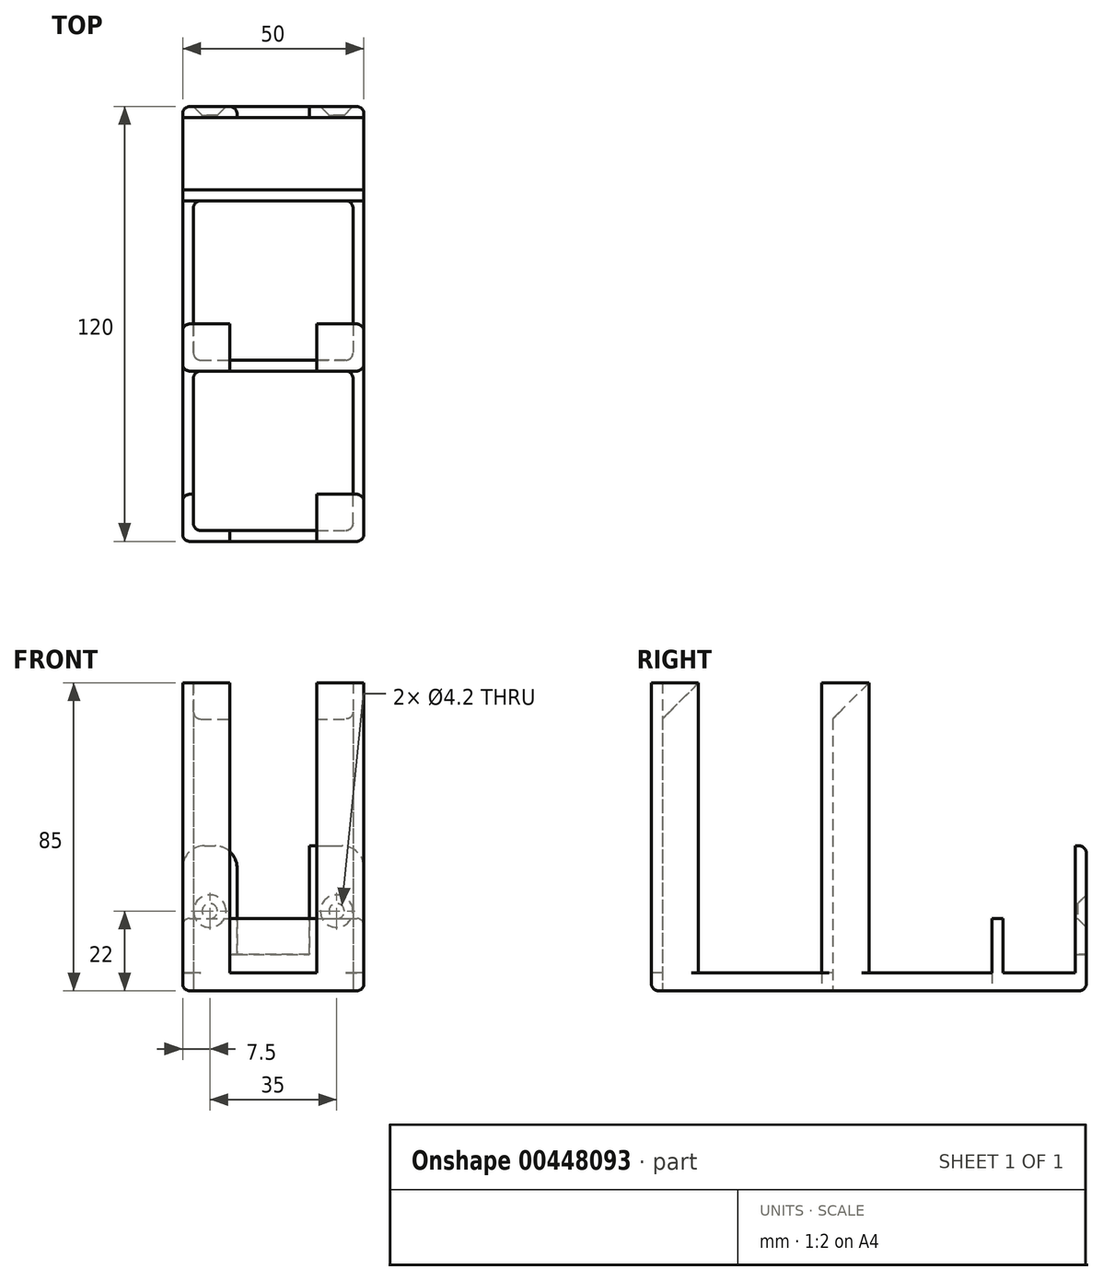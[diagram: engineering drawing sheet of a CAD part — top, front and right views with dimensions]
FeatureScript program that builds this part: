
annotation { "Feature Type Name" : "Feature", "Feature Type Description" : "" }
export const myFeature = defineFeature(function(context is Context, id is Id, definition is map)
    precondition{}
    {
        {
            var Q0;
            Q0=qCreatedBy(makeId("Top.planeOp"),FACE);
            var sketch = newSketch(context, id + "F0", { "sketchPlane" : qUnion([Q0])});
            skLineSegment(sketch, "E0.bottom", {"start": v(-22, 45.5) * mm, "end": v(22, 45.5) * mm});
            skLineSegment(sketch, "E0.top", {"start": v(-22, 1.5) * mm, "end": v(22, 1.5) * mm});
            skLineSegment(sketch, "E0.left", {"start": v(-22, 45.5) * mm, "end": v(-22, 1.5) * mm});
            skLineSegment(sketch, "E0.right", {"start": v(22, 45.5) * mm, "end": v(22, 1.5) * mm});
            skLineSegment(sketch, "E1.MirrorCS", {"start": v(-22, -1.5) * mm, "end": v(22, -1.5) * mm});
            skLineSegment(sketch, "E2.MirrorCS", {"start": v(-22, -45.5) * mm, "end": v(-22, -1.5) * mm});
            skLineSegment(sketch, "E3.MirrorCS", {"start": v(-22, -45.5) * mm, "end": v(22, -45.5) * mm});
            skLineSegment(sketch, "E4.MirrorCS", {"start": v(22, -45.5) * mm, "end": v(22, -1.5) * mm});
            skLineSegment(sketch, "E5.bottom", {"start": v(-25, 71.5) * mm, "end": v(25, 71.5) * mm});
            skLineSegment(sketch, "E5.top", {"start": v(-25, -48.5) * mm, "end": v(25, -48.5) * mm});
            skLineSegment(sketch, "E5.left", {"start": v(-25, 71.5) * mm, "end": v(-25, -48.5) * mm});
            skLineSegment(sketch, "E5.right", {"start": v(25, 71.5) * mm, "end": v(25, -48.5) * mm});
            skSolve(sketch);
        }
        {
            var Q0;
            Q0=makeQuery(id+"F0.imprint","IMPRINT",FACE,{"disambiguationData":[TD([[makeQuery(id+"F0.imprint","IMPRINT",EDGE,{"derivedFrom":sQuery(id+"F0.wireOp",EDGE,"E0.bottom")}),1.0]])]});
            extrude(context, id + "F1", {"entities" : qUnion([Q0]), "depth" : 5 * mm});
        }
        {
            var Q0;
            Q0=makeQuery(id+"F1.opExtrude","CAP_FACE",FACE,{"disambiguationData":[OSD([sQuery(id+"F0.wireOp",EDGE,"E0.bottom"),sQuery(id+"F0.wireOp",EDGE,"E0.top"),sQuery(id+"F0.wireOp",EDGE,"E0.left"),sQuery(id+"F0.wireOp",EDGE,"E0.right"),sQuery(id+"F0.wireOp",EDGE,"E1.MirrorCS"),sQuery(id+"F0.wireOp",EDGE,"E2.MirrorCS"),sQuery(id+"F0.wireOp",EDGE,"E3.MirrorCS"),sQuery(id+"F0.wireOp",EDGE,"E4.MirrorCS"),sQuery(id+"F0.wireOp",EDGE,"E5.bottom"),sQuery(id+"F0.wireOp",EDGE,"E5.top"),sQuery(id+"F0.wireOp",EDGE,"E5.left"),sQuery(id+"F0.wireOp",EDGE,"E5.right")])],"isStart":false});
            var sketch = newSketch(context, id + "F2", { "sketchPlane" : qUnion([Q0])});
            skLineSegment(sketch, "E6.bottom", {"start": v(-25, 71.5) * mm, "end": v(25, 71.5) * mm});
            skLineSegment(sketch, "E6.top", {"start": v(-25, 68.5) * mm, "end": v(25, 68.5) * mm});
            skLineSegment(sketch, "E6.left", {"start": v(-25, 71.5) * mm, "end": v(-25, 68.5) * mm});
            skLineSegment(sketch, "E6.right", {"start": v(25, 71.5) * mm, "end": v(25, 68.5) * mm});
            skLineSegment(sketch, "E7.bottom", {"start": v(-25, 48.5) * mm, "end": v(25, 48.5) * mm});
            skLineSegment(sketch, "E7.top", {"start": v(-25, 45.5) * mm, "end": v(25, 45.5) * mm});
            skLineSegment(sketch, "E7.left", {"start": v(-25, 48.5) * mm, "end": v(-25, 45.5) * mm});
            skLineSegment(sketch, "E7.right", {"start": v(25, 48.5) * mm, "end": v(25, 45.5) * mm});
            skLineSegment(sketch, "E8", {"start": v(-25, 11.5) * mm, "end": v(-22, 11.5) * mm});
            skLineSegment(sketch, "E9", {"start": v(-22, 11.5) * mm, "end": v(-22, 1.5) * mm});
            skLineSegment(sketch, "E10", {"start": v(-22, 1.5) * mm, "end": v(-12, 1.5) * mm});
            skLineSegment(sketch, "E11", {"start": v(-12, 1.5) * mm, "end": v(-12, -1.5) * mm});
            skLineSegment(sketch, "E12", {"start": v(-12, -1.5) * mm, "end": v(-25, -1.5) * mm});
            skLineSegment(sketch, "E13", {"start": v(-25, -1.5) * mm, "end": v(-25, 11.5) * mm});
            skLineSegment(sketch, "E14.MirrorCS", {"start": v(12, 1.5) * mm, "end": v(12, -1.5) * mm});
            skLineSegment(sketch, "E15.MirrorCS", {"start": v(22, 1.5) * mm, "end": v(12, 1.5) * mm});
            skLineSegment(sketch, "E16.MirrorCS", {"start": v(12, -1.5) * mm, "end": v(25, -1.5) * mm});
            skLineSegment(sketch, "E17.MirrorCS", {"start": v(25, -1.5) * mm, "end": v(25, 11.5) * mm});
            skLineSegment(sketch, "E18.MirrorCS", {"start": v(25, 11.5) * mm, "end": v(22, 11.5) * mm});
            skLineSegment(sketch, "E19.MirrorCS", {"start": v(22, 11.5) * mm, "end": v(22, 1.5) * mm});
            skLineSegment(sketch, "E20.0.1.0", {"start": v(-25, -35.5) * mm, "end": v(-22, -35.5) * mm});
            skLineSegment(sketch, "E20.0.1.1", {"start": v(-25, -48.5) * mm, "end": v(-25, -35.5) * mm});
            skLineSegment(sketch, "E20.0.1.2", {"start": v(-22, -35.5) * mm, "end": v(-22, -45.5) * mm});
            skLineSegment(sketch, "E20.0.1.3", {"start": v(-22, -45.5) * mm, "end": v(-12, -45.5) * mm});
            skLineSegment(sketch, "E20.0.1.4", {"start": v(-12, -45.5) * mm, "end": v(-12, -48.5) * mm});
            skLineSegment(sketch, "E20.0.1.5", {"start": v(-12, -48.5) * mm, "end": v(-25, -48.5) * mm});
            skLineSegment(sketch, "E20.0.1.6", {"start": v(12, -48.5) * mm, "end": v(25, -48.5) * mm});
            skLineSegment(sketch, "E20.0.1.7", {"start": v(12, -45.5) * mm, "end": v(12, -48.5) * mm});
            skLineSegment(sketch, "E20.0.1.8", {"start": v(22, -45.5) * mm, "end": v(12, -45.5) * mm});
            skLineSegment(sketch, "E20.0.1.9", {"start": v(25, -48.5) * mm, "end": v(25, -35.5) * mm});
            skLineSegment(sketch, "E20.0.1.10", {"start": v(22, -35.5) * mm, "end": v(22, -45.5) * mm});
            skLineSegment(sketch, "E20.0.1.11", {"start": v(25, -35.5) * mm, "end": v(22, -35.5) * mm});
            skLineSegment(sketch, "E20.direction1", {"start": v(-25, 11.5) * mm, "end": v(-8.5, 11.8) * mm, "construction": true});
            skLineSegment(sketch, "E20.direction2", {"start": v(-25, 11.5) * mm, "end": v(-25, -35.5) * mm, "construction": true});
            skSolve(sketch);
        }
        {
            var Q0;
            Q0=makeQuery(id+"F2.imprint","IMPRINT",FACE,{"disambiguationData":[TD([[makeQuery(id+"F2.imprint","IMPRINT",EDGE,{"derivedFrom":sQuery(id+"F2.wireOp",EDGE,"E6.bottom")}),-1.0]])]});
            extrude(context, id + "F3", {"entities" : qUnion([Q0]), "operationType" : NewBodyOperationType.ADD, "depth" : 35 * mm});
        }
        {
            var Q0;
            Q0=makeQuery(id+"F2.imprint","IMPRINT",FACE,{"disambiguationData":[TD([[makeQuery(id+"F2.imprint","IMPRINT",EDGE,{"derivedFrom":sQuery(id+"F2.wireOp",EDGE,"E7.bottom")}),-1.0]])]});
            extrude(context, id + "F4", {"entities" : qUnion([Q0]), "operationType" : NewBodyOperationType.ADD, "depth" : 15 * mm});
        }
        {
            var Q0;
            Q0=makeQuery(id+"F2.imprint","IMPRINT",FACE,{"disambiguationData":[TD([[makeQuery(id+"F2.imprint","IMPRINT",EDGE,{"derivedFrom":sQuery(id+"F2.wireOp",EDGE,"E8")}),-1.0]])]});
            var Q1;
            {var subQ2=sQuery(id+"F2.wireOp",EDGE,"E14.MirrorCS");Q1=makeQuery(id+"F2.imprint","IMPRINT",FACE,{"disambiguationData":[TD([[makeQuery(id+"F2.imprint","IMPRINT",EDGE,{"derivedFrom":subQ2}),1.0]])]});}
            var Q2;
            Q2=makeQuery(id+"F2.imprint","IMPRINT",FACE,{"disambiguationData":[TD([[makeQuery(id+"F2.imprint","IMPRINT",EDGE,{"derivedFrom":sQuery(id+"F2.wireOp",EDGE,"E20.0.1.0")}),-1.0]])]});
            var Q3;
            Q3=makeQuery(id+"F2.imprint","IMPRINT",FACE,{"disambiguationData":[TD([[makeQuery(id+"F2.imprint","IMPRINT",EDGE,{"derivedFrom":sQuery(id+"F2.wireOp",EDGE,"E20.0.1.6")}),1.0]])]});
            extrude(context, id + "F5", {"entities" : qUnion([Q0, Q1, Q2, Q3]), "operationType" : NewBodyOperationType.ADD, "depth" : 80 * mm});
        }
        {
            var Q0;
            Q0=makeQuery(id+"F5.boolean.opBoolean","MERGE",FACE,{"derivedFrom":[makeQuery(id+"F1.opExtrude","SWEPT_FACE",FACE,{"disambiguationData":[OSD([sQuery(id+"F0.wireOp",EDGE,"E0.top")])]}),makeQuery(id+"F5.opExtrude","SWEPT_FACE",FACE,{"disambiguationData":[OSD([sQuery(id+"F2.wireOp",EDGE,"E10")])]}),makeQuery(id+"F5.opExtrude","SWEPT_FACE",FACE,{"disambiguationData":[OSD([sQuery(id+"F2.wireOp",EDGE,"E15.MirrorCS")])]})]});
            var sketch = newSketch(context, id + "F6", { "sketchPlane" : qUnion([Q0])});
            skLineSegment(sketch, "E21.bottom", {"start": v(22, 85) * mm, "end": v(12, 85) * mm});
            skLineSegment(sketch, "E21.top", {"start": v(22, 75) * mm, "end": v(12, 75) * mm});
            skLineSegment(sketch, "E21.left", {"start": v(22, 85) * mm, "end": v(22, 75) * mm});
            skLineSegment(sketch, "E21.right", {"start": v(12, 85) * mm, "end": v(12, 75) * mm});
            skLineSegment(sketch, "E22.MirrorCS", {"start": v(-22, 75) * mm, "end": v(-12, 75) * mm});
            skLineSegment(sketch, "E23.MirrorCS", {"start": v(-22, 85) * mm, "end": v(-22, 75) * mm});
            skLineSegment(sketch, "E24.MirrorCS", {"start": v(-22, 85) * mm, "end": v(-12, 85) * mm});
            skLineSegment(sketch, "E25.MirrorCS", {"start": v(-12, 85) * mm, "end": v(-12, 75) * mm});
            skSolve(sketch);
        }
        {
            var Q0;
            Q0=makeQuery(id+"F5.boolean.opBoolean","MERGE",FACE,{"derivedFrom":[makeQuery(id+"F1.opExtrude","SWEPT_FACE",FACE,{"disambiguationData":[OSD([sQuery(id+"F0.wireOp",EDGE,"E3.MirrorCS")])]}),makeQuery(id+"F5.opExtrude","SWEPT_FACE",FACE,{"disambiguationData":[OSD([sQuery(id+"F2.wireOp",EDGE,"E20.0.1.3")])]}),makeQuery(id+"F5.opExtrude","SWEPT_FACE",FACE,{"disambiguationData":[OSD([sQuery(id+"F2.wireOp",EDGE,"E20.0.1.8")])]})]});
            var sketch = newSketch(context, id + "F7", { "sketchPlane" : qUnion([Q0])});
            skLineSegment(sketch, "E26.0", {"start": v(22, 75) * mm, "end": v(12, 75) * mm});
            skLineSegment(sketch, "E27.bottom", {"start": v(12, 75) * mm, "end": v(22, 75) * mm});
            skLineSegment(sketch, "E27.top", {"start": v(12, 85) * mm, "end": v(22, 85) * mm});
            skLineSegment(sketch, "E27.left", {"start": v(12, 75) * mm, "end": v(12, 85) * mm});
            skLineSegment(sketch, "E27.right", {"start": v(22, 75) * mm, "end": v(22, 85) * mm});
            skLineSegment(sketch, "E28.MirrorCS", {"start": v(-12, 75) * mm, "end": v(-22, 75) * mm});
            skLineSegment(sketch, "E29.MirrorCS", {"start": v(-12, 75) * mm, "end": v(-12, 85) * mm});
            skLineSegment(sketch, "E30.MirrorCS", {"start": v(-12, 85) * mm, "end": v(-22, 85) * mm});
            skLineSegment(sketch, "E31.MirrorCS", {"start": v(-22, 75) * mm, "end": v(-22, 85) * mm});
            skSolve(sketch);
        }
        {
            var Q0;
            Q0=makeQuery(id+"F6.imprint","IMPRINT",FACE,{"disambiguationData":[TD([[makeQuery(id+"F6.imprint","IMPRINT",EDGE,{"derivedFrom":sQuery(id+"F6.wireOp",EDGE,"E22.MirrorCS")}),1.0]])]});
            var Q1;
            Q1=makeQuery(id+"F6.imprint","IMPRINT",FACE,{"disambiguationData":[TD([[makeQuery(id+"F6.imprint","IMPRINT",EDGE,{"derivedFrom":sQuery(id+"F6.wireOp",EDGE,"E21.bottom")}),1.0]])]});
            var Q2;
            Q2=makeQuery(id+"F7.imprint","IMPRINT",FACE,{"disambiguationData":[TD([[makeQuery(id+"F7.imprint","IMPRINT",EDGE,{"derivedFrom":sQuery(id+"F7.wireOp",EDGE,"E27.bottom")}),1.0]])]});
            var Q3;
            Q3=makeQuery(id+"F7.imprint","IMPRINT",FACE,{"disambiguationData":[TD([[makeQuery(id+"F7.imprint","IMPRINT",EDGE,{"derivedFrom":sQuery(id+"F7.wireOp",EDGE,"E28.MirrorCS")}),-1.0]])]});
            extrude(context, id + "F8", {"entities" : qUnion([Q0, Q1, Q2, Q3]), "operationType" : NewBodyOperationType.ADD, "depth" : 10 * mm});
        }
        {
            var Q0;
            Q0=makeQuery(id+"F8.opExtrude","CAP_EDGE",EDGE,{"disambiguationData":[OSD([sQuery(id+"F6.wireOp",EDGE,"E21.top")])],"isStart":false});
            var Q1;
            Q1=makeQuery(id+"F8.opExtrude","CAP_EDGE",EDGE,{"disambiguationData":[OSD([sQuery(id+"F7.wireOp",EDGE,"E27.bottom")])],"isStart":false});
            var Q2;
            Q2=makeQuery(id+"F8.opExtrude","CAP_EDGE",EDGE,{"disambiguationData":[OSD([sQuery(id+"F6.wireOp",EDGE,"E22.MirrorCS")])],"isStart":false});
            var Q3;
            Q3=makeQuery(id+"F8.opExtrude","CAP_EDGE",EDGE,{"disambiguationData":[OSD([sQuery(id+"F7.wireOp",EDGE,"E28.MirrorCS")])],"isStart":false});
            chamfer(context, id + "F9", {"entities" : qUnion([Q0, Q1, Q2, Q3]), "width" : 10 * mm, "tangentPropagation" : true});
        }
        {
            var Q0;
            Q0=makeQuery(id+"F3.boolean.opBoolean","MERGE",FACE,{"derivedFrom":[makeQuery(id+"F1.opExtrude","SWEPT_FACE",FACE,{"disambiguationData":[OSD([sQuery(id+"F0.wireOp",EDGE,"E5.bottom")])]}),makeQuery(id+"F3.opExtrude","SWEPT_FACE",FACE,{"disambiguationData":[OSD([sQuery(id+"F2.wireOp",EDGE,"E6.bottom")])]})]});
            var sketch = newSketch(context, id + "F10", { "sketchPlane" : qUnion([Q0])});
            skLineSegment(sketch, "E32.bottom", {"start": v(-10, 40) * mm, "end": v(10, 40) * mm});
            skLineSegment(sketch, "E32.top", {"start": v(-10, 10) * mm, "end": v(10, 10) * mm});
            skLineSegment(sketch, "E32.left", {"start": v(-10, 40) * mm, "end": v(-10, 10) * mm});
            skLineSegment(sketch, "E32.right", {"start": v(10, 40) * mm, "end": v(10, 10) * mm});
            skSolve(sketch);
        }
        {
            var Q0;
            Q0=makeQuery(id+"F10.imprint","IMPRINT",FACE,{"disambiguationData":[TD([[makeQuery(id+"F10.imprint","IMPRINT",EDGE,{"derivedFrom":sQuery(id+"F10.wireOp",EDGE,"E32.bottom")}),1.0]])]});
            extrude(context, id + "F11", {"entities" : qUnion([Q0]), "operationType" : NewBodyOperationType.REMOVE, "endBound" : BoundingType.UP_TO_NEXT, "oppositeDirection" : true, "depth" : 25 * mm});
        }
        {
            var Q0;
            Q0=makeQuery(id+"F3.opExtrude","CAP_EDGE",EDGE,{"disambiguationData":[OSD([sQuery(id+"F2.wireOp",EDGE,"E6.right")])],"isStart":false});
            var Q1;
            Q1=makeQuery(id+"F11.boolean.opBoolean","COPY",EDGE,{"derivedFrom":makeQuery(id+"F11.opExtrude","SWEPT_EDGE",EDGE,{"disambiguationData":[OSD([sQuery(id+"F2.wireOp",EDGE,"E6.bottom"),sQuery(id+"F10.wireOp",EDGE,"E32.bottom"),sQuery(id+"F10.wireOp",EDGE,"E32.left")])]})});
            var Q2;
            Q2=makeQuery(id+"F11.boolean.opBoolean","COPY",EDGE,{"derivedFrom":makeQuery(id+"F11.opExtrude","SWEPT_EDGE",EDGE,{"disambiguationData":[OSD([sQuery(id+"F2.wireOp",EDGE,"E6.bottom"),sQuery(id+"F10.wireOp",EDGE,"E32.bottom"),sQuery(id+"F10.wireOp",EDGE,"E32.right")])]})});
            var Q3;
            Q3=makeQuery(id+"F3.opExtrude","CAP_EDGE",EDGE,{"disambiguationData":[OSD([sQuery(id+"F2.wireOp",EDGE,"E6.left")])],"isStart":false});
            fillet(context, id + "F12", {"entities" : qUnion([Q0, Q1, Q2, Q3]), "radius" : 6 * mm, "tangentPropagation" : true, "allowEdgeOverflow" : false});
        }
        {
            var Q0;
            Q0=makeQuery(id+"F3.boolean.opBoolean","MERGE",EDGE,{"derivedFrom":[makeQuery(id+"F1.opExtrude","SWEPT_EDGE",EDGE,{"disambiguationData":[OSD([sQuery(id+"F0.wireOp",EDGE,"E5.bottom"),sQuery(id+"F0.wireOp",EDGE,"E5.left")])]}),makeQuery(id+"F3.opExtrude","SWEPT_EDGE",EDGE,{"disambiguationData":[OSD([sQuery(id+"F2.wireOp",EDGE,"E6.bottom"),sQuery(id+"F2.wireOp",EDGE,"E6.left")])]})]});
            var Q1;
            Q1=makeQuery(id+"F3.boolean.opBoolean","MERGE",EDGE,{"derivedFrom":[makeQuery(id+"F1.opExtrude","SWEPT_EDGE",EDGE,{"disambiguationData":[OSD([sQuery(id+"F0.wireOp",EDGE,"E5.bottom"),sQuery(id+"F0.wireOp",EDGE,"E5.right")])]}),makeQuery(id+"F3.opExtrude","SWEPT_EDGE",EDGE,{"disambiguationData":[OSD([sQuery(id+"F2.wireOp",EDGE,"E6.bottom"),sQuery(id+"F2.wireOp",EDGE,"E6.right")])]})]});
            var Q2;
            Q2=makeQuery(id+"F1.opExtrude","CAP_EDGE",EDGE,{"disambiguationData":[OSD([sQuery(id+"F0.wireOp",EDGE,"E5.right")])],"isStart":true});
            var Q3;
            Q3=makeQuery(id+"F1.opExtrude","CAP_EDGE",EDGE,{"disambiguationData":[OSD([sQuery(id+"F0.wireOp",EDGE,"E5.top")])],"isStart":true});
            var Q4;
            Q4=makeQuery(id+"F1.opExtrude","CAP_EDGE",EDGE,{"disambiguationData":[OSD([sQuery(id+"F0.wireOp",EDGE,"E5.left")])],"isStart":true});
            var Q5;
            Q5=makeQuery(id+"F1.opExtrude","CAP_EDGE",EDGE,{"disambiguationData":[OSD([sQuery(id+"F0.wireOp",EDGE,"E5.bottom")])],"isStart":true});
            var Q6;
            Q6=makeQuery(id+"F5.boolean.opBoolean","MERGE",EDGE,{"derivedFrom":[makeQuery(id+"F1.opExtrude","SWEPT_EDGE",EDGE,{"disambiguationData":[OSD([sQuery(id+"F0.wireOp",EDGE,"E0.top"),sQuery(id+"F0.wireOp",EDGE,"E0.right")])]}),makeQuery(id+"F5.opExtrude","SWEPT_EDGE",EDGE,{"disambiguationData":[OSD([sQuery(id+"F2.wireOp",EDGE,"E15.MirrorCS"),sQuery(id+"F2.wireOp",EDGE,"E19.MirrorCS")])]})]});
            var Q7;
            Q7=makeQuery(id+"F5.boolean.opBoolean","MERGE",EDGE,{"derivedFrom":[makeQuery(id+"F1.opExtrude","SWEPT_EDGE",EDGE,{"disambiguationData":[OSD([sQuery(id+"F0.wireOp",EDGE,"E3.MirrorCS"),sQuery(id+"F0.wireOp",EDGE,"E4.MirrorCS")])]}),makeQuery(id+"F5.opExtrude","SWEPT_EDGE",EDGE,{"disambiguationData":[OSD([sQuery(id+"F2.wireOp",EDGE,"E20.0.1.8"),sQuery(id+"F2.wireOp",EDGE,"E20.0.1.10")])]})]});
            var Q8;
            Q8=makeQuery(id+"F5.boolean.opBoolean","MERGE",EDGE,{"derivedFrom":[makeQuery(id+"F1.opExtrude","SWEPT_EDGE",EDGE,{"disambiguationData":[OSD([sQuery(id+"F0.wireOp",EDGE,"E2.MirrorCS"),sQuery(id+"F0.wireOp",EDGE,"E3.MirrorCS")])]}),makeQuery(id+"F5.opExtrude","SWEPT_EDGE",EDGE,{"disambiguationData":[OSD([sQuery(id+"F2.wireOp",EDGE,"E20.0.1.2"),sQuery(id+"F2.wireOp",EDGE,"E20.0.1.3")])]})]});
            var Q9;
            Q9=makeQuery(id+"F5.boolean.opBoolean","MERGE",EDGE,{"derivedFrom":[makeQuery(id+"F1.opExtrude","SWEPT_EDGE",EDGE,{"disambiguationData":[OSD([sQuery(id+"F0.wireOp",EDGE,"E0.top"),sQuery(id+"F0.wireOp",EDGE,"E0.left")])]}),makeQuery(id+"F5.opExtrude","SWEPT_EDGE",EDGE,{"disambiguationData":[OSD([sQuery(id+"F2.wireOp",EDGE,"E9"),sQuery(id+"F2.wireOp",EDGE,"E10")])]})]});
            var Q10;
            Q10=makeQuery(id+"F5.boolean.opBoolean","MERGE",EDGE,{"derivedFrom":[makeQuery(id+"F1.opExtrude","SWEPT_EDGE",EDGE,{"disambiguationData":[OSD([sQuery(id+"F0.wireOp",EDGE,"E5.top"),sQuery(id+"F0.wireOp",EDGE,"E5.left")])]}),makeQuery(id+"F5.opExtrude","SWEPT_EDGE",EDGE,{"disambiguationData":[OSD([sQuery(id+"F2.wireOp",EDGE,"E20.0.1.1"),sQuery(id+"F2.wireOp",EDGE,"E20.0.1.5")])]})]});
            var Q11;
            Q11=makeQuery(id+"F5.boolean.opBoolean","MERGE",EDGE,{"derivedFrom":[makeQuery(id+"F1.opExtrude","SWEPT_EDGE",EDGE,{"disambiguationData":[OSD([sQuery(id+"F0.wireOp",EDGE,"E5.top"),sQuery(id+"F0.wireOp",EDGE,"E5.right")])]}),makeQuery(id+"F5.opExtrude","SWEPT_EDGE",EDGE,{"disambiguationData":[OSD([sQuery(id+"F2.wireOp",EDGE,"E20.0.1.6"),sQuery(id+"F2.wireOp",EDGE,"E20.0.1.9")])]})]});
            var Q12;
            Q12=makeQuery(id+"F5.opExtrude","SWEPT_EDGE",EDGE,{"disambiguationData":[OSD([sQuery(id+"F0.wireOp",EDGE,"E5.right"),sQuery(id+"F2.wireOp",EDGE,"E16.MirrorCS"),sQuery(id+"F2.wireOp",EDGE,"E17.MirrorCS")])]});
            var Q13;
            Q13=makeQuery(id+"F5.opExtrude","SWEPT_EDGE",EDGE,{"disambiguationData":[OSD([sQuery(id+"F0.wireOp",EDGE,"E5.left"),sQuery(id+"F2.wireOp",EDGE,"E12"),sQuery(id+"F2.wireOp",EDGE,"E13")])]});
            var Q14;
            Q14=makeQuery(id+"F4.opExtrude","CAP_EDGE",EDGE,{"disambiguationData":[OSD([sQuery(id+"F2.wireOp",EDGE,"E7.right")])],"isStart":false});
            var Q15;
            Q15=makeQuery(id+"F4.opExtrude","CAP_EDGE",EDGE,{"disambiguationData":[OSD([sQuery(id+"F2.wireOp",EDGE,"E7.left")])],"isStart":false});
            var Q16;
            Q16=makeQuery(id+"F1.opExtrude","SWEPT_EDGE",EDGE,{"disambiguationData":[OSD([sQuery(id+"F0.wireOp",EDGE,"E0.bottom"),sQuery(id+"F0.wireOp",EDGE,"E0.left")])]});
            var Q17;
            Q17=makeQuery(id+"F1.opExtrude","SWEPT_EDGE",EDGE,{"disambiguationData":[OSD([sQuery(id+"F0.wireOp",EDGE,"E1.MirrorCS"),sQuery(id+"F0.wireOp",EDGE,"E2.MirrorCS")])]});
            var Q18;
            Q18=makeQuery(id+"F1.opExtrude","SWEPT_EDGE",EDGE,{"disambiguationData":[OSD([sQuery(id+"F0.wireOp",EDGE,"E1.MirrorCS"),sQuery(id+"F0.wireOp",EDGE,"E4.MirrorCS")])]});
            var Q19;
            Q19=makeQuery(id+"F1.opExtrude","SWEPT_EDGE",EDGE,{"disambiguationData":[OSD([sQuery(id+"F0.wireOp",EDGE,"E0.bottom"),sQuery(id+"F0.wireOp",EDGE,"E0.right")])]});
            var Q20;
            Q20=makeQuery(id+"F5.opExtrude","SWEPT_EDGE",EDGE,{"disambiguationData":[OSD([sQuery(id+"F0.wireOp",EDGE,"E5.right"),sQuery(id+"F2.wireOp",EDGE,"E20.0.1.9"),sQuery(id+"F2.wireOp",EDGE,"E20.0.1.11")])]});
            var Q21;
            Q21=makeQuery(id+"F5.opExtrude","SWEPT_EDGE",EDGE,{"disambiguationData":[OSD([sQuery(id+"F0.wireOp",EDGE,"E5.right"),sQuery(id+"F2.wireOp",EDGE,"E17.MirrorCS"),sQuery(id+"F2.wireOp",EDGE,"E18.MirrorCS")])]});
            var Q22;
            Q22=makeQuery(id+"F5.opExtrude","SWEPT_EDGE",EDGE,{"disambiguationData":[OSD([sQuery(id+"F0.wireOp",EDGE,"E5.left"),sQuery(id+"F2.wireOp",EDGE,"E8"),sQuery(id+"F2.wireOp",EDGE,"E13")])]});
            var Q23;
            Q23=makeQuery(id+"F5.opExtrude","SWEPT_EDGE",EDGE,{"disambiguationData":[OSD([sQuery(id+"F0.wireOp",EDGE,"E5.left"),sQuery(id+"F2.wireOp",EDGE,"E20.0.1.0"),sQuery(id+"F2.wireOp",EDGE,"E20.0.1.1")])]});
            fillet(context, id + "F13", {"entities" : qUnion([Q0, Q1, Q2, Q3, Q4, Q5, Q6, Q7, Q8, Q9, Q10, Q11, Q12, Q13, Q14, Q15, Q16, Q17, Q18, Q19, Q20, Q21, Q22, Q23]), "radius" : 2 * mm, "tangentPropagation" : true, "allowEdgeOverflow" : false});
        }
        {
            var Q0;
            Q0=makeQuery(id+"F3.boolean.opBoolean","MERGE",FACE,{"derivedFrom":[makeQuery(id+"F1.opExtrude","SWEPT_FACE",FACE,{"disambiguationData":[OSD([sQuery(id+"F0.wireOp",EDGE,"E5.bottom")])]}),makeQuery(id+"F3.opExtrude","SWEPT_FACE",FACE,{"disambiguationData":[OSD([sQuery(id+"F2.wireOp",EDGE,"E6.bottom")])]})]});
            var sketch = newSketch(context, id + "F14", { "sketchPlane" : qUnion([Q0])});
            skPoint(sketch, "E33", {"position": v(-17.5, 22) * mm});
            skPoint(sketch, "E33.positionSnap0", {"position": v(-12, 22) * mm});
            skPoint(sketch, "E33.positionSnap1", {"position": v(-17.5, 38) * mm});
            skPoint(sketch, "E34.MirrorP", {"position": v(17.5, 22) * mm});
            skSolve(sketch);
        }
        {
            var Q0;
            Q0=sQuery(id+"F14.wireOp",VERTEX,"E33");
            var Q1;
            Q1=sQuery(id+"F14.wireOp",VERTEX,"E34.MirrorP");
            var Q2;
            Q2=makeQuery(id+"F1.opExtrude","SWEPT_BODY",BODY,{"disambiguationData":[OSD([sQuery(id+"F0.wireOp",EDGE,"E0.bottom"),sQuery(id+"F0.wireOp",EDGE,"E0.top"),sQuery(id+"F0.wireOp",EDGE,"E0.left"),sQuery(id+"F0.wireOp",EDGE,"E0.right"),sQuery(id+"F0.wireOp",EDGE,"E1.MirrorCS"),sQuery(id+"F0.wireOp",EDGE,"E2.MirrorCS"),sQuery(id+"F0.wireOp",EDGE,"E3.MirrorCS"),sQuery(id+"F0.wireOp",EDGE,"E4.MirrorCS"),sQuery(id+"F0.wireOp",EDGE,"E5.bottom"),sQuery(id+"F0.wireOp",EDGE,"E5.top"),sQuery(id+"F0.wireOp",EDGE,"E5.left"),sQuery(id+"F0.wireOp",EDGE,"E5.right")])]});
            hole(context, id + "F15", {"style" : HoleStyle.C_SINK, "endStyle" : HoleEndStyle.BLIND, "holeDiameter" : 4.2 * mm, "cSinkDiameter" : 8.96 * mm, "cSinkAngle" : 90 * degree, "holeDepth" : 12 * mm, "isTappedThrough" : true, "tappedDepth" : 12 * mm, "tapClearance" : 3, "locations" : qUnion([Q0, Q1]), "scope" : qUnion([Q2])});
        }
    });
